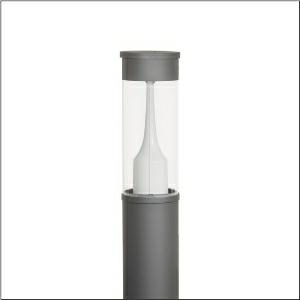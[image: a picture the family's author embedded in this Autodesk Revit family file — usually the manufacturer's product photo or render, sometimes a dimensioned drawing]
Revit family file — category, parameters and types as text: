
# Revit family: city-light_260_iq___p1_0a_5xa5295nf14h_1e18
name_source: partatom
category: Lighting Fixtures
units: mm (PartAtom-declared; Revit-internal decimal feet)

## family parameters
Cut with Voids When Loaded = No
Host = Face
Light Source = No
Part Type = Normal
Room Calculation Point = No
Round Connector Dimension = Use Diameter
Shared = No

## types (1)
- --- (1 x LED, 1510 lm, 11.8 W, 2700K)
    Apparent Load = 12 VA
    CIE Flux Codes = 32 61 90 93 100
    Color Rendering = 70
    Color Temperature = 2700K
    Default Elevation = 1800 mm
    Description = City-Light 260 iQ, light pillar, Module 540 iQ-SR, primary light control with 3 zone facetted reflector, of plastic, silver coated, highly specular, structured, primary optical cover: cover, of PMMA, transparent, partly coated, light distribution: P1.0a, primary light characteristic: strongly asymmetric, LED, High Power LED, rated luminous flux: 1.510lm, luminous efficacy: 128lm/W, light colour: 727, colour temperature: 2700K, control gear: iQ Street-Remote, control: pre-setting: logarithmic dimming characteristic, Street-Remote, Auto-Match, Temp-Guard, Lumen-Switch, Night-Set, Smart-Wire, Light-Fading, Desk-Remote (wireless, voltage-free reading and setting of iQ features in the workshop via application-optimized NFC function/RFID function), optimised constant luminous flux control (CLO 2.0), with terminal, 6-pole, max. 2.5mm², mains connection: 230..240V, AC, 50/60Hz, start of lifetime: 12W, end of service life: 12W, reduction: 6W, luminaire housing, cylindrical, of extruded aluminium section, coated, Siteco® metallic grey (DB 702S), length: 2.600mm, diameter: 200mm, Module 540 iQ-SR, traffic white (RAL 9016), equipment: standard, protection rating (complete): IP65, insulation class (complete): insulation class II (safety insulation), certification: CE, ENEC, VDE, packaging unit: 1 piece

Light Distribution: P1.0a
    Height = 500 mm
    Lamp = 1 x LED
    Lamp Light Flux = 1510 lm
    Lamp Power = 11.8 W
    Lamp count = 1
    Length = 200 mm  [stored 0.656168 ft]
    Luminous efficacy = 128 lm/W
    Manufacturer = Siteco
    ModVariant = No
    Model = 5XA5295NF14H
    Mounting Place = Floor
    Mounting Type = Freestanding
    Number of Poles = 1
    OnlyDefault = Yes
    Power Factor = 1
    Product Name = City-Light 260 iQ | P1.0a
    Product group = light pillar
    ProductGroupID = 1301
    Protection Class = Protection class II
    Protection Degree = IP 65
    RLX_Detail_Level = 1
    RLX_Emergency_Light_Flux = 0 lm
    RLX_Emergency_Type = 0
    RLX_Emergency_Type_DB = No
    RlxData = <blob elided: 52745 chars, md5=299226dc>
    Socket = socket
    Standby Power = 0 W
    System Light Flux = 1510 lm
    System Power = 12 W
    Type Comments = factory setting: luminous flux: 100 % | dim-lin: 254 | 472 mA
    Type Image = l_1006918.jpg
    URL = http://relux.com
    VarID = @adj_174631
    Voltage = 0 V
    Weight = 0.00 kg
    Width = 0 mm  [stored 0 ft]

note: [stored X ft] marks values corroborated as IEEE doubles in the binary element streams (Revit-internal decimal feet)

## geometry (parser evidence)
native form markers: Blend x4, Sweep x9
no freeform markers — native parametric forms only
